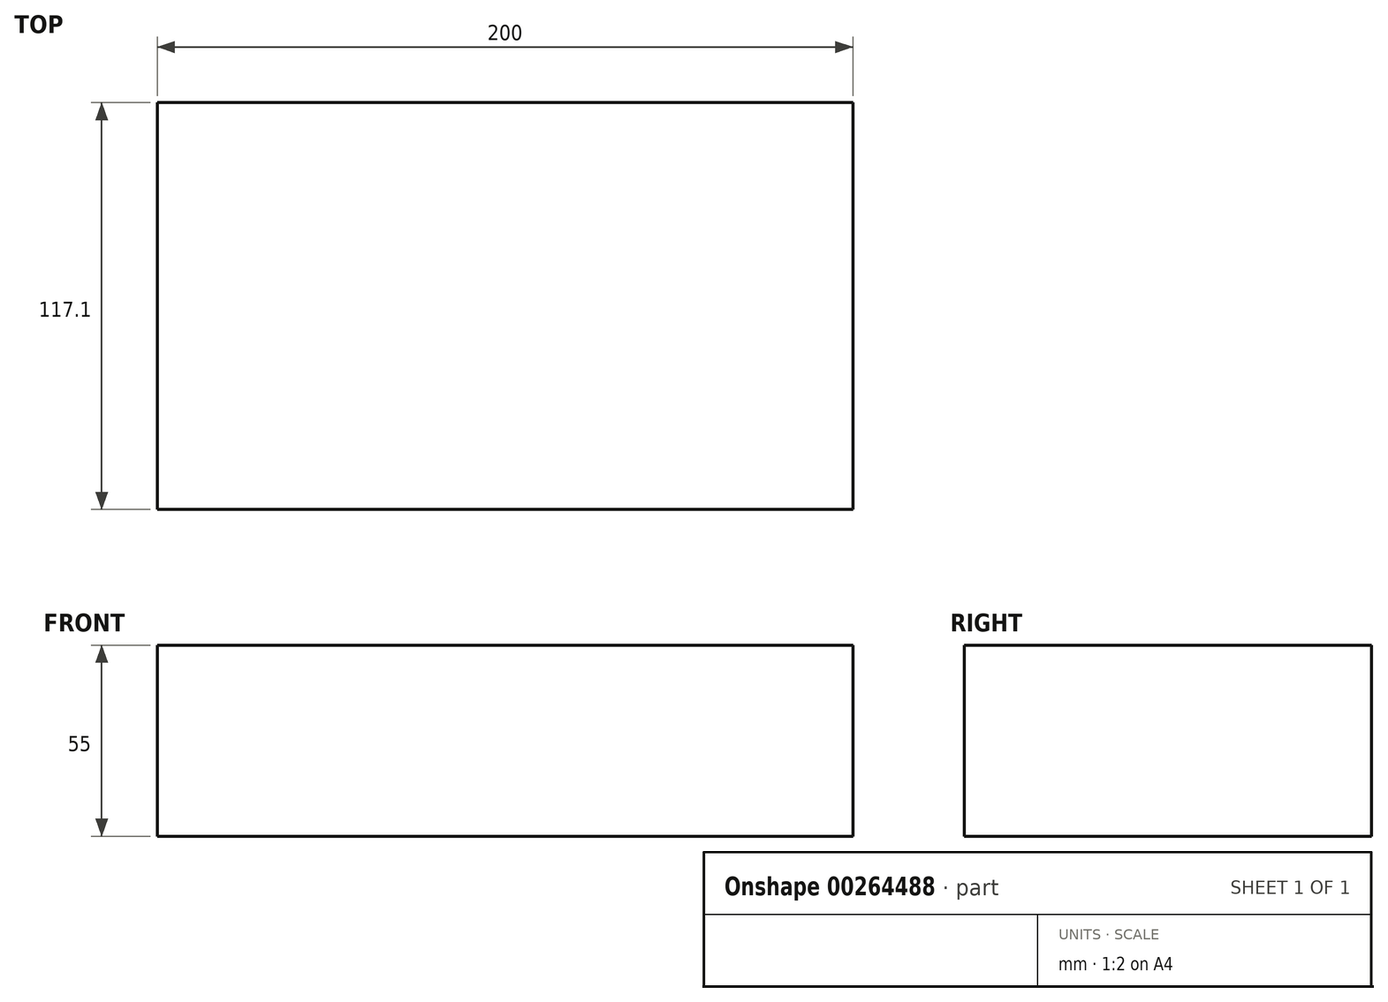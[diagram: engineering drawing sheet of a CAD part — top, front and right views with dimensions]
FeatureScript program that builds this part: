
annotation { "Feature Type Name" : "Feature", "Feature Type Description" : "" }
export const myFeature = defineFeature(function(context is Context, id is Id, definition is map)
    precondition{}
    {
        {
            var Q0;
            Q0=qCreatedBy(makeId("Top.planeOp"),FACE);
            var sketch = newSketch(context, id + "F0", { "sketchPlane" : qUnion([Q0])});
            skLineSegment(sketch, "E0.bottom", {"start": v(-100, 58.55) * mm, "end": v(100, 58.55) * mm});
            skLineSegment(sketch, "E0.top", {"start": v(-100, -58.55) * mm, "end": v(100, -58.55) * mm});
            skLineSegment(sketch, "E0.left", {"start": v(-100, 58.55) * mm, "end": v(-100, -58.55) * mm});
            skLineSegment(sketch, "E0.right", {"start": v(100, 58.55) * mm, "end": v(100, -58.55) * mm});
            skLineSegment(sketch, "E1", {"start": v(0, 58.55) * mm, "end": v(0, -58.55) * mm, "construction": true});
            skLineSegment(sketch, "E2", {"start": v(-100, 0) * mm, "end": v(100, 0) * mm, "construction": true});
            skSolve(sketch);
        }
        {
            var Q0;
            Q0 = qSketchRegion(id + "F0", true);
            extrude(context, id + "F1", {"entities" : qUnion([Q0]), "depth" : 55 * mm});
        }
    });
